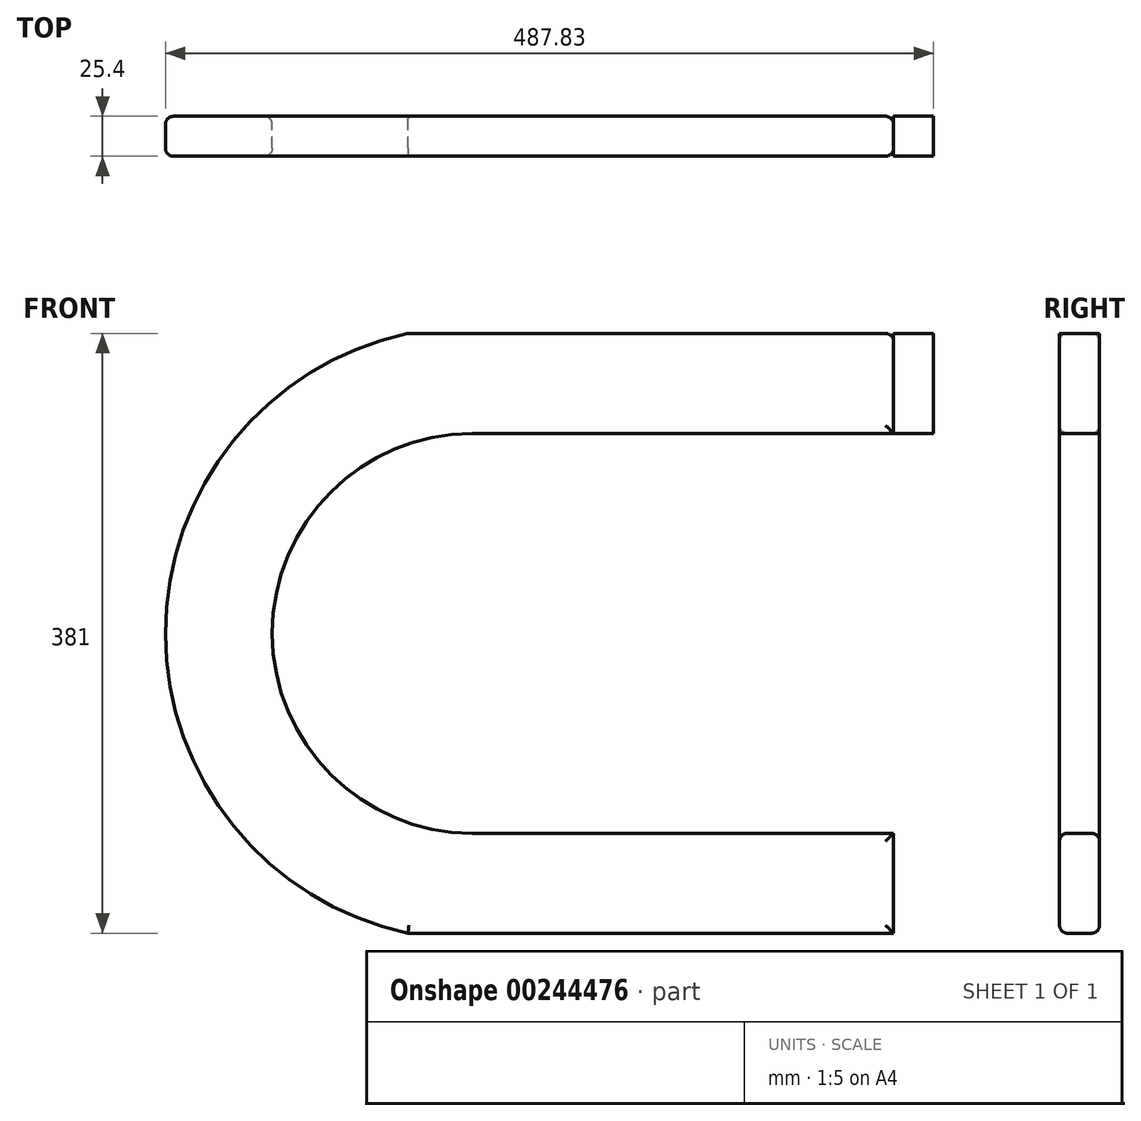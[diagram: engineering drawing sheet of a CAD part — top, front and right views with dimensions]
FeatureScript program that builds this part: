
annotation { "Feature Type Name" : "Feature", "Feature Type Description" : "" }
export const myFeature = defineFeature(function(context is Context, id is Id, definition is map)
    precondition{}
    {
        {
            var Q0;
            Q0=qCreatedBy(makeId("Front.planeOp"),FACE);
            var sketch = newSketch(context, id + "F0", { "sketchPlane" : qUnion([Q0])});
            skArc(sketch, "E0", {"start": v(0, 127) * mm, "mid": v(-127, 0) * mm, "end": v(0, -127) * mm});
            skPoint(sketch, "E1.middle", {"position": v(-174.58, 17.68) * mm});
            skLineSegment(sketch, "E2.bottom", {"start": v(-40.79, 190.5) * mm, "end": v(204.1, 190.5) * mm});
            skLineSegment(sketch, "E2.top", {"start": v(-40.79, -190.5) * mm, "end": v(204.1, -190.5) * mm});
            skLineSegment(sketch, "E3", {"start": v(0, 127) * mm, "end": v(204.1, 127) * mm});
            skLineSegment(sketch, "E4", {"start": v(0, -127) * mm, "end": v(204.1, -127) * mm});
            skArc(sketch, "E5", {"start": v(-40.79, 190.5) * mm, "mid": v(-194.82, 0) * mm, "end": v(-40.79, -190.5) * mm});
            skPoint(sketch, "E2.left.start.orphan", {"position": v(-204.1, 190.5) * mm});
            skPoint(sketch, "E6.orphan", {"position": v(-204.1, -190.5) * mm});
            skLineSegment(sketch, "E7.trimOffspring", {"start": v(204.1, -127) * mm, "end": v(204.1, -190.5) * mm});
            skLineSegment(sketch, "E8", {"start": v(204.1, 190.5) * mm, "end": v(204.1, 127) * mm});
            skLineSegment(sketch, "E9.bottom", {"start": v(204.1, 190.5) * mm, "end": v(267.6, 190.5) * mm});
            skLineSegment(sketch, "E9.top", {"start": v(204.1, 127) * mm, "end": v(267.6, 127) * mm});
            skLineSegment(sketch, "E9.right", {"start": v(267.6, 190.5) * mm, "end": v(267.6, 127) * mm});
            skLineSegment(sketch, "E10.bottom", {"start": v(204.1, -127) * mm, "end": v(267.6, -127) * mm});
            skLineSegment(sketch, "E10.top", {"start": v(204.1, -190.5) * mm, "end": v(267.6, -190.5) * mm});
            skLineSegment(sketch, "E10.right", {"start": v(267.6, -127) * mm, "end": v(267.6, -190.5) * mm});
            skSolve(sketch);
        }
        {
            var Q0;
            Q0=makeQuery(id+"F0.imprint","IMPRINT",FACE,{"disambiguationData":[TD([[makeQuery(id+"F0.imprint","IMPRINT",EDGE,{"derivedFrom":sQuery(id+"F0.wireOp",EDGE,"E0")}),-1.0]])]});
            var Q1;
            Q1=makeQuery(id+"F0.imprint","IMPRINT",FACE,{"disambiguationData":[TD([[makeQuery(id+"F0.imprint","IMPRINT",EDGE,{"derivedFrom":sQuery(id+"F0.wireOp",EDGE,"E9.bottom")}),-1.0]])]});
            var Q2;
            Q2=makeQuery(id+"F0.imprint","IMPRINT",FACE,{"disambiguationData":[TD([[makeQuery(id+"F0.imprint","IMPRINT",EDGE,{"derivedFrom":sQuery(id+"F0.wireOp",EDGE,"E10.bottom")}),-1.0]])]});
            extrude(context, id + "F1", {"entities" : qUnion([Q0, Q1, Q2]), "depth" : 25.4 * mm});
        }
        {
            var Q0;
            Q0=makeQuery(id+"F1.opExtrude","SWEPT_FACE",FACE,{"disambiguationData":[OSD([sQuery(id+"F0.wireOp",EDGE,"E9.right")])]});
            extrude(context, id + "F2", {"entities" : qUnion([Q0]), "depth" : 25.4 * mm});
        }
        {
            var Q0;
            Q0=makeQuery(id+"F1.opExtrude","CAP_FACE",FACE,{"disambiguationData":[OSD([sQuery(id+"F0.wireOp",EDGE,"E0"),sQuery(id+"F0.wireOp",EDGE,"E2.bottom"),sQuery(id+"F0.wireOp",EDGE,"E2.top"),sQuery(id+"F0.wireOp",EDGE,"E3"),sQuery(id+"F0.wireOp",EDGE,"E4"),sQuery(id+"F0.wireOp",EDGE,"E5"),sQuery(id+"F0.wireOp",EDGE,"E9.bottom"),sQuery(id+"F0.wireOp",EDGE,"E9.top"),sQuery(id+"F0.wireOp",EDGE,"E9.right"),sQuery(id+"F0.wireOp",EDGE,"E10.bottom"),sQuery(id+"F0.wireOp",EDGE,"E10.top"),sQuery(id+"F0.wireOp",EDGE,"E10.right")])],"isStart":false});
            var Q1;
            Q1=makeQuery(id+"F1.opExtrude","SWEPT_FACE",FACE,{"disambiguationData":[OSD([sQuery(id+"F0.wireOp",EDGE,"E2.bottom"),sQuery(id+"F0.wireOp",EDGE,"E9.bottom")])]});
            var Q2;
            Q2=makeQuery(id+"F1.opExtrude","CAP_EDGE",EDGE,{"disambiguationData":[OSD([sQuery(id+"F0.wireOp",EDGE,"E4"),sQuery(id+"F0.wireOp",EDGE,"E10.bottom")])],"isStart":true});
            var Q3;
            Q3=makeQuery(id+"F1.opExtrude","CAP_EDGE",EDGE,{"disambiguationData":[OSD([sQuery(id+"F0.wireOp",EDGE,"E0")])],"isStart":false});
            var Q4;
            Q4=makeQuery(id+"F1.opExtrude","SWEPT_FACE",FACE,{"disambiguationData":[OSD([sQuery(id+"F0.wireOp",EDGE,"E0")])]});
            var Q5;
            Q5=makeQuery(id+"F1.opExtrude","CAP_FACE",FACE,{"disambiguationData":[OSD([sQuery(id+"F0.wireOp",EDGE,"E0"),sQuery(id+"F0.wireOp",EDGE,"E2.bottom"),sQuery(id+"F0.wireOp",EDGE,"E2.top"),sQuery(id+"F0.wireOp",EDGE,"E3"),sQuery(id+"F0.wireOp",EDGE,"E4"),sQuery(id+"F0.wireOp",EDGE,"E5"),sQuery(id+"F0.wireOp",EDGE,"E9.bottom"),sQuery(id+"F0.wireOp",EDGE,"E9.top"),sQuery(id+"F0.wireOp",EDGE,"E9.right"),sQuery(id+"F0.wireOp",EDGE,"E10.bottom"),sQuery(id+"F0.wireOp",EDGE,"E10.top"),sQuery(id+"F0.wireOp",EDGE,"E10.right")])],"isStart":true});
            fillet(context, id + "F3", {"entities" : qUnion([Q0, Q1, Q2, Q3, Q4, Q5]), "radius" : 5.08 * mm, "tangentPropagation" : true, "allowEdgeOverflow" : false});
        }
    });
